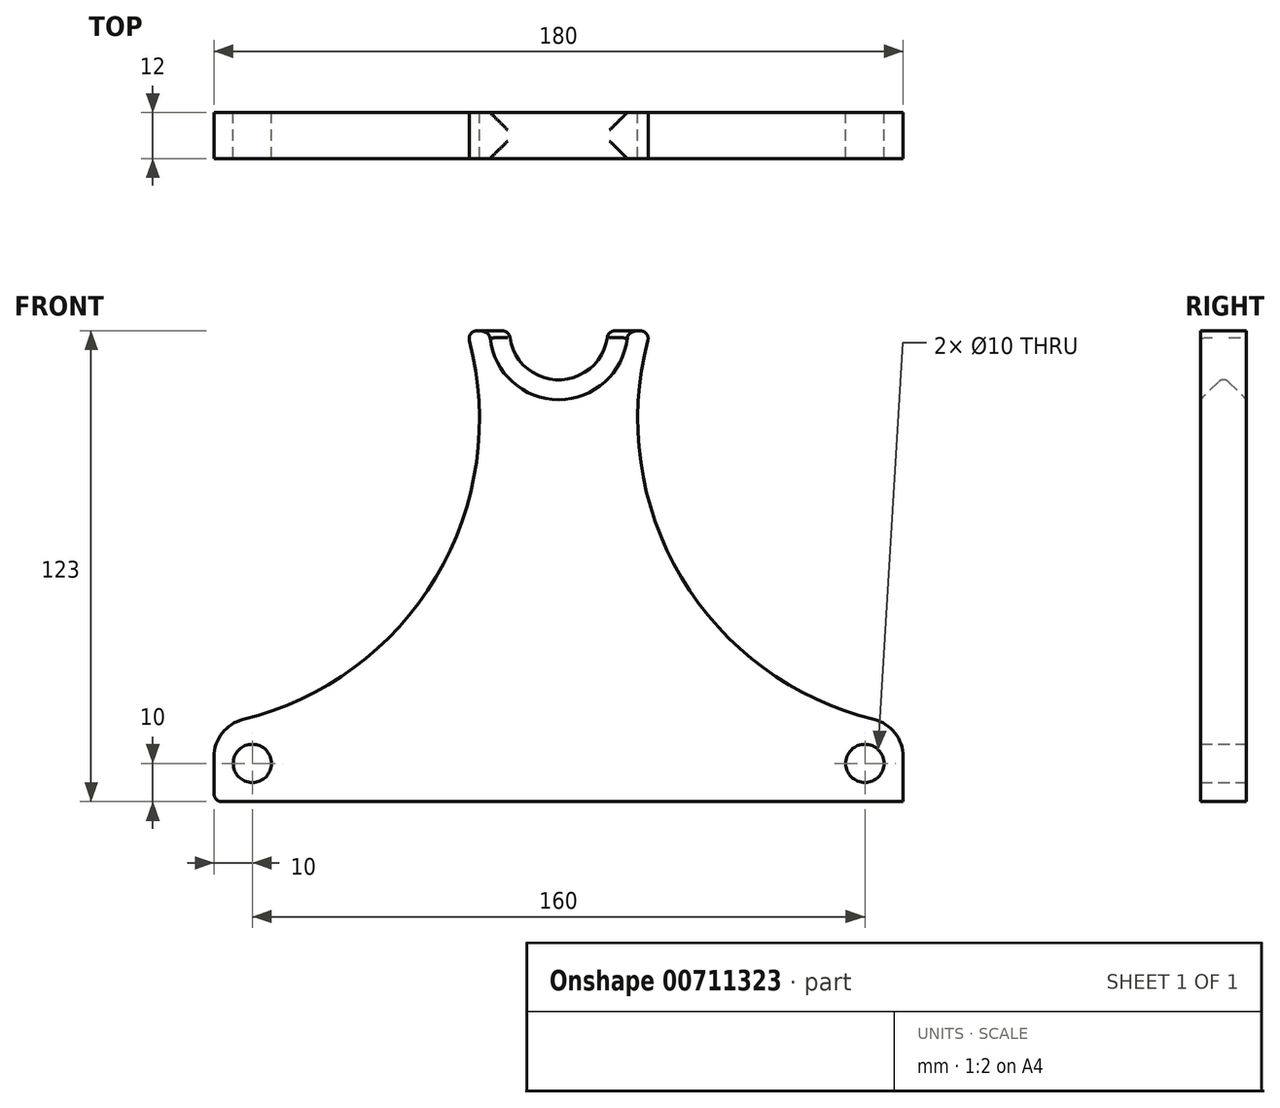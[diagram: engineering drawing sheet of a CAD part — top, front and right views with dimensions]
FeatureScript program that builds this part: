
annotation { "Feature Type Name" : "Feature", "Feature Type Description" : "" }
export const myFeature = defineFeature(function(context is Context, id is Id, definition is map)
    precondition{}
    {
        {
            var Q0;
            Q0=qCreatedBy(makeId("Front.planeOp"),FACE);
            var sketch = newSketch(context, id + "F0", { "sketchPlane" : qUnion([Q0])});
            skLineSegment(sketch, "E0", {"start": v(0, 111) * mm, "end": v(0, 0) * mm});
            skLineSegment(sketch, "E1", {"start": v(-12, 123) * mm, "end": v(-24, 123) * mm});
            skLineSegment(sketch, "E2", {"start": v(0, 0) * mm, "end": v(-90, 0) * mm});
            skLineSegment(sketch, "E3", {"start": v(-90, 0) * mm, "end": v(-90, 11.76) * mm});
            skArc(sketch, "E4", {"start": v(-90, 20) * mm, "mid": v(-86.16, 20.64) * mm, "end": v(-82.36, 21.47) * mm, "construction": true});
            skArc(sketch, "E5", {"start": v(-12, 123) * mm, "mid": v(-8.49, 114.51) * mm, "end": v(0, 111) * mm});
            skLineSegment(sketch, "E6.MirrorCS", {"start": v(0, 0) * mm, "end": v(90, 0) * mm});
            skLineSegment(sketch, "E7.MirrorCS", {"start": v(12, 123) * mm, "end": v(24, 123) * mm});
            skLineSegment(sketch, "E8.MirrorCS", {"start": v(0, 111) * mm, "end": v(0, 0) * mm, "construction": true});
            skArc(sketch, "E9.MirrorCS", {"start": v(12, 123) * mm, "mid": v(8.49, 114.51) * mm, "end": v(0, 111) * mm});
            skCircle(sketch, "E10", {"center": v(-80, 10) * mm, "radius": 5 * mm});
            skPoint(sketch, "E11.visualSharp", {"position": v(-90, 20) * mm});
            skArc(sketch, "E11.filletArc", {"start": v(-82.36, 21.47) * mm, "mid": v(-87.86, 17.94) * mm, "end": v(-90, 11.76) * mm});
            skArc(sketch, "E12", {"start": v(-82.36, 21.47) * mm, "mid": v(-31.41, 59.72) * mm, "end": v(-24, 123) * mm});
            skLineSegment(sketch, "E13", {"start": v(-90, 11.76) * mm, "end": v(-90, 20) * mm, "construction": true});
            skArc(sketch, "E14.MirrorCS", {"start": v(82.36, 21.47) * mm, "mid": v(31.41, 59.72) * mm, "end": v(24, 123) * mm});
            skArc(sketch, "E15.MirrorCS", {"start": v(82.36, 21.47) * mm, "mid": v(87.86, 17.94) * mm, "end": v(90, 11.76) * mm});
            skLineSegment(sketch, "E16.MirrorCS", {"start": v(90, 0) * mm, "end": v(90, 11.76) * mm});
            skCircle(sketch, "E17.MirrorC", {"center": v(80, 10) * mm, "radius": 5 * mm});
            skSolve(sketch);
        }
        {
            var Q0;
            Q0=makeQuery(id+"F0.imprint","IMPRINT",FACE,{"disambiguationData":[TD([[makeQuery(id+"F0.imprint","IMPRINT",EDGE,{"derivedFrom":sQuery(id+"F0.wireOp",EDGE,"E1")}),1.0]])]});
            var Q1;
            Q1=makeQuery(id+"F0.imprint","IMPRINT",FACE,{"disambiguationData":[TD([[makeQuery(id+"F0.imprint","IMPRINT",EDGE,{"derivedFrom":sQuery(id+"F0.wireOp",EDGE,"6afeca36-bedc-414c-91b2-24b9e0b04e360.MirrorCS")}),1.0]])]});
            var Q2;
            Q2=makeQuery(id+"F0.imprint","IMPRINT",FACE,{"disambiguationData":[TD([[makeQuery(id+"F0.imprint","IMPRINT",EDGE,{"derivedFrom":sQuery(id+"F0.wireOp",EDGE,"E0")}),1.0]])]});
            extrude(context, id + "F1", {"entities" : qUnion([Q0, Q1, Q2]), "endBound" : BoundingType.SYMMETRIC, "depth" : 12 * mm, "offsetDistance" : 25 * mm});
        }
        {
            var Q0;
            Q0=makeQuery(id+"F1.opExtrude","CAP_EDGE",EDGE,{"disambiguationData":[OSD([sQuery(id+"F0.wireOp",EDGE,"E5"),sQuery(id+"F0.wireOp",EDGE,"E9.MirrorCS")])],"isStart":false});
            var Q1;
            Q1=makeQuery(id+"F1.opExtrude","CAP_EDGE",EDGE,{"disambiguationData":[OSD([sQuery(id+"F0.wireOp",EDGE,"E5"),sQuery(id+"F0.wireOp",EDGE,"E9.MirrorCS")])],"isStart":true});
            chamfer(context, id + "F2", {"entities" : qUnion([Q0, Q1]), "width" : 6 * mm, "tangentPropagation" : true});
        }
        {
            var Q0;
            Q0=makeQuery(id+"F1.opExtrude","SWEPT_EDGE",EDGE,{"disambiguationData":[OSD([sQuery(id+"F0.wireOp",EDGE,"E3"),sQuery(id+"F0.wireOp",EDGE,"E4")])]});
            var Q1;
            Q1=makeQuery(id+"F1.opExtrude","SWEPT_EDGE",EDGE,{"disambiguationData":[OSD([sQuery(id+"F0.wireOp",EDGE,"6afeca36-bedc-414c-91b2-24b9e0b04e360.MirrorCS"),sQuery(id+"F0.wireOp",EDGE,"6afeca36-bedc-414c-91b2-24b9e0b04e365.MirrorCS")])]});
            var Q2;
            Q2=makeQuery(id+"F1.opExtrude","SWEPT_EDGE",EDGE,{"disambiguationData":[OSD([sQuery(id+"F0.wireOp",EDGE,"E1"),sQuery(id+"F0.wireOp",EDGE,"E4")])]});
            var Q3;
            {var subQ0=sQuery(id+"F0.wireOp",EDGE,"E9.MirrorCS");var subQ1=sQuery(id+"F0.wireOp",EDGE,"E5");Q3=makeQuery(id+"F2.opChamfer","BLEND_EDGE",EDGE,{"blendedFrom":[makeQuery(id+"F1.opExtrude","CAP_EDGE",EDGE,{"disambiguationData":[OSD([subQ1,subQ0])],"isStart":true}),makeQuery(id+"F1.opExtrude","CAP_EDGE",EDGE,{"disambiguationData":[OSD([subQ1,subQ0])],"isStart":false})],"blendedInto":[]});}
            var Q4;
            Q4=makeQuery(id+"F1.opExtrude","SWEPT_EDGE",EDGE,{"disambiguationData":[OSD([sQuery(id+"F0.wireOp",EDGE,"E7.MirrorCS"),sQuery(id+"F0.wireOp",EDGE,"6afeca36-bedc-414c-91b2-24b9e0b04e365.MirrorCS")])]});
            var Q5;
            Q5=makeQuery(id+"F2.opChamfer","BLEND_EDGE",EDGE,{"blendedFrom":[makeQuery(id+"F1.opExtrude","CAP_EDGE",EDGE,{"disambiguationData":[OSD([sQuery(id+"F0.wireOp",EDGE,"E5"),sQuery(id+"F0.wireOp",EDGE,"E9.MirrorCS")])],"isStart":true}),makeQuery(id+"F1.opExtrude","SWEPT_FACE",FACE,{"disambiguationData":[OSD([sQuery(id+"F0.wireOp",EDGE,"E7.MirrorCS")])]})],"blendedInto":[makeQuery(id+"F1.opExtrude","SWEPT_FACE",FACE,{"disambiguationData":[OSD([sQuery(id+"F0.wireOp",EDGE,"E7.MirrorCS")])]})]});
            var Q6;
            Q6=makeQuery(id+"F2.opChamfer","BLEND_EDGE",EDGE,{"blendedFrom":[makeQuery(id+"F1.opExtrude","CAP_EDGE",EDGE,{"disambiguationData":[OSD([sQuery(id+"F0.wireOp",EDGE,"E5"),sQuery(id+"F0.wireOp",EDGE,"E9.MirrorCS")])],"isStart":false}),makeQuery(id+"F1.opExtrude","SWEPT_FACE",FACE,{"disambiguationData":[OSD([sQuery(id+"F0.wireOp",EDGE,"E7.MirrorCS")])]})],"blendedInto":[makeQuery(id+"F1.opExtrude","SWEPT_FACE",FACE,{"disambiguationData":[OSD([sQuery(id+"F0.wireOp",EDGE,"E7.MirrorCS")])]})]});
            var Q7;
            Q7=makeQuery(id+"F2.opChamfer","BLEND_EDGE",EDGE,{"blendedFrom":[makeQuery(id+"F1.opExtrude","CAP_EDGE",EDGE,{"disambiguationData":[OSD([sQuery(id+"F0.wireOp",EDGE,"E5"),sQuery(id+"F0.wireOp",EDGE,"E9.MirrorCS")])],"isStart":true}),makeQuery(id+"F1.opExtrude","SWEPT_FACE",FACE,{"disambiguationData":[OSD([sQuery(id+"F0.wireOp",EDGE,"E1")])]})],"blendedInto":[makeQuery(id+"F1.opExtrude","SWEPT_FACE",FACE,{"disambiguationData":[OSD([sQuery(id+"F0.wireOp",EDGE,"E1")])]})]});
            var Q8;
            Q8=makeQuery(id+"F2.opChamfer","BLEND_EDGE",EDGE,{"blendedFrom":[makeQuery(id+"F1.opExtrude","CAP_EDGE",EDGE,{"disambiguationData":[OSD([sQuery(id+"F0.wireOp",EDGE,"E5"),sQuery(id+"F0.wireOp",EDGE,"E9.MirrorCS")])],"isStart":false}),makeQuery(id+"F1.opExtrude","SWEPT_FACE",FACE,{"disambiguationData":[OSD([sQuery(id+"F0.wireOp",EDGE,"E1")])]})],"blendedInto":[makeQuery(id+"F1.opExtrude","SWEPT_FACE",FACE,{"disambiguationData":[OSD([sQuery(id+"F0.wireOp",EDGE,"E1")])]})]});
            fillet(context, id + "F3", {"entities" : qUnion([Q0, Q1, Q2, Q3, Q4, Q5, Q6, Q7, Q8]), "radius" : 2 * mm, "tangentPropagation" : true, "allowEdgeOverflow" : false});
        }
    });
